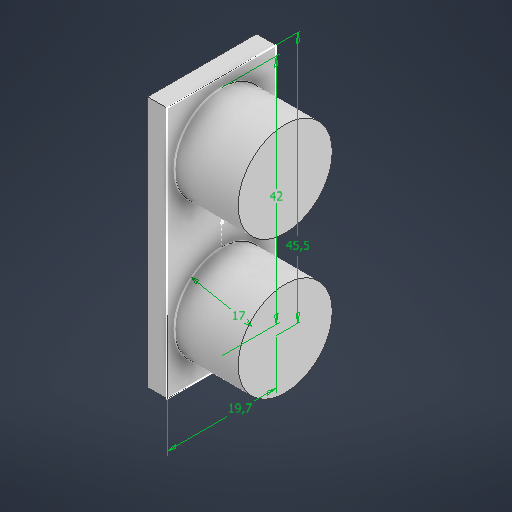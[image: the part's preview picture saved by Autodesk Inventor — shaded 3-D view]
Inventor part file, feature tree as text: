
AUTODESK INVENTOR PART (.ipt)
format: ipt  version: 2025.2 (Build 292293000, 293)  size: 212,480 bytes
history: native  units: mm
features: extrude x2, sketch x1
ambient origin geometry x8: Origin, YZ Plane, XZ Plane, XY Plane, X Axis, Y Axis, Z Axis, Center Point
bodies: Solid1 (feature_tree)
feature tree (3):
  sketch  "Sketch1"  dims[d0=45.5mm d1=17.0mm d3=42.0mm d4=19.7mm d5=3.5mm d6=0.0mm d7=11.5mm d8=0.0mm]
  extrude  "Extrusion1"  Depth=11.5mm
  extrude  "Extrusion2"  Depth=11.5mm
